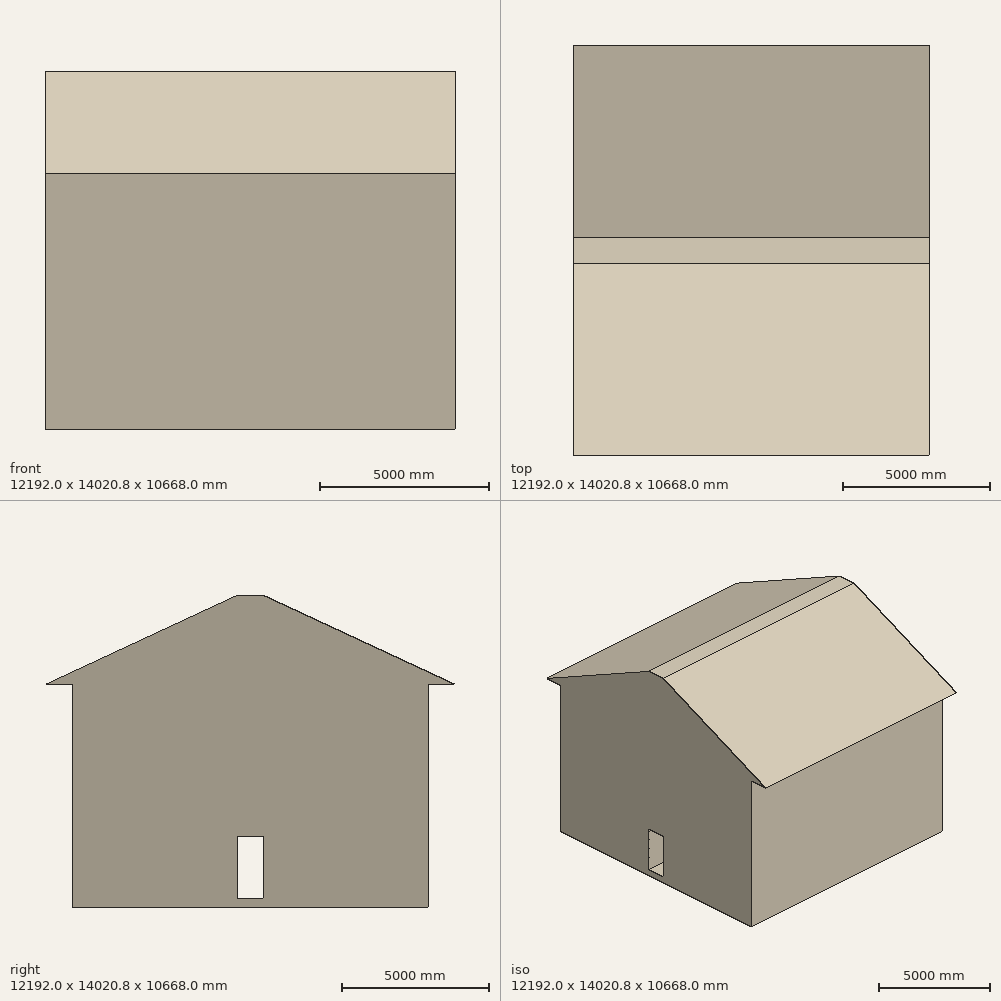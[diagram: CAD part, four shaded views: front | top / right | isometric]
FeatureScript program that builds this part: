
annotation { "Feature Type Name" : "Feature", "Feature Type Description" : "" }
export const myFeature = defineFeature(function(context is Context, id is Id, definition is map)
    precondition{}
    {
        {
            var Q0;
            Q0=qCreatedBy(makeId("Right.planeOp"),FACE);
            var sketch = newSketch(context, id + "F0", { "sketchPlane" : qUnion([Q0])});
            skLineSegment(sketch, "E0", {"start": v(0, 0) * mm, "end": v(-6096, 0) * mm});
            skLineSegment(sketch, "E1", {"start": v(0, 0) * mm, "end": v(6096, 0) * mm});
            skLineSegment(sketch, "E2", {"start": v(0, 0) * mm, "end": v(0, 3048) * mm, "construction": true});
            skLineSegment(sketch, "E3", {"start": v(-6096, 0) * mm, "end": v(0, 3048) * mm});
            skLineSegment(sketch, "E4", {"start": v(6096, 0) * mm, "end": v(0, 3048) * mm});
            skLineSegment(sketch, "E5", {"start": v(-6096, 0) * mm, "end": v(-6096, -7315.2) * mm});
            skLineSegment(sketch, "E6", {"start": v(-6096, -7315.2) * mm, "end": v(6096, -7315.2) * mm});
            skLineSegment(sketch, "E7", {"start": v(6096, 0) * mm, "end": v(6096, -7315.2) * mm});
            skLineSegment(sketch, "E8", {"start": v(-6096, -7315.2) * mm, "end": v(-6096, -7620) * mm});
            skLineSegment(sketch, "E9", {"start": v(-6096, -7620) * mm, "end": v(6096, -7620) * mm});
            skLineSegment(sketch, "E10", {"start": v(6096, -7620) * mm, "end": v(6096, -7315.2) * mm});
            skLineSegment(sketch, "E11", {"start": v(0, -7315.2) * mm, "end": v(-457.2, -7315.2) * mm});
            skLineSegment(sketch, "E12", {"start": v(0, -7315.2) * mm, "end": v(457.2, -7315.2) * mm});
            skLineSegment(sketch, "E13", {"start": v(-457.2, -7315.2) * mm, "end": v(-457.2, -5181.6) * mm});
            skLineSegment(sketch, "E14", {"start": v(-457.2, -5181.6) * mm, "end": v(457.2, -5181.6) * mm});
            skLineSegment(sketch, "E15", {"start": v(457.2, -5181.6) * mm, "end": v(457.2, -7315.2) * mm});
            skLineSegment(sketch, "E16", {"start": v(-6096, 0) * mm, "end": v(-7010.4, 0) * mm});
            skLineSegment(sketch, "E17", {"start": v(6096, 0) * mm, "end": v(7010.4, 0) * mm});
            skLineSegment(sketch, "E18", {"start": v(0, 3048) * mm, "end": v(457.2, 3048) * mm});
            skLineSegment(sketch, "E19", {"start": v(0, 3048) * mm, "end": v(-457.2, 3048) * mm});
            skLineSegment(sketch, "E20", {"start": v(-7010.4, 0) * mm, "end": v(-457.2, 3048) * mm});
            skLineSegment(sketch, "E21", {"start": v(7010.4, 0) * mm, "end": v(457.2, 3048) * mm});
            skLineSegment(sketch, "E22.bottom", {"start": v(-2743.2, -914.4) * mm, "end": v(-914.4, -914.4) * mm});
            skLineSegment(sketch, "E22.top", {"start": v(-2743.2, -2133.6) * mm, "end": v(-914.4, -2133.6) * mm});
            skLineSegment(sketch, "E22.left", {"start": v(-2743.2, -914.4) * mm, "end": v(-2743.2, -2133.6) * mm});
            skLineSegment(sketch, "E22.right", {"start": v(-914.4, -914.4) * mm, "end": v(-914.4, -2133.6) * mm});
            skLineSegment(sketch, "E23.bottom", {"start": v(3449.56, -218.05) * mm, "end": v(5278.36, -218.05) * mm});
            skLineSegment(sketch, "E23.top", {"start": v(3449.56, -1742.05) * mm, "end": v(5278.36, -1742.05) * mm});
            skLineSegment(sketch, "E23.left", {"start": v(3449.56, -218.05) * mm, "end": v(3449.56, -1742.05) * mm});
            skLineSegment(sketch, "E23.right", {"start": v(5278.36, -218.05) * mm, "end": v(5278.36, -1742.05) * mm});
            skLineSegment(sketch, "E24.bottom", {"start": v(-3558.79, -5153.92) * mm, "end": v(-2034.79, -5153.92) * mm});
            skLineSegment(sketch, "E24.top", {"start": v(-3558.79, -6677.92) * mm, "end": v(-2034.79, -6677.92) * mm});
            skLineSegment(sketch, "E24.left", {"start": v(-3558.79, -5153.92) * mm, "end": v(-3558.79, -6677.92) * mm});
            skLineSegment(sketch, "E24.right", {"start": v(-2034.79, -5153.92) * mm, "end": v(-2034.79, -6677.92) * mm});
            skLineSegment(sketch, "E25.left", {"start": v(-3558.79, -5153.92) * mm, "end": v(-3558.79, -5153.92) * mm});
            skCircle(sketch, "E26.cCircle", {"center": v(3162.99, -4421.52) * mm, "radius": 957.11 * mm, "construction": true});
            skLineSegment(sketch, "E26.0", {"start": v(4268.14, -4428.14) * mm, "end": v(3709.83, -5381.92) * mm});
            skLineSegment(sketch, "E26.1", {"start": v(3709.83, -5381.92) * mm, "end": v(2604.67, -5375.3) * mm});
            skLineSegment(sketch, "E26.2", {"start": v(2604.67, -5375.3) * mm, "end": v(2057.83, -4414.9) * mm});
            skLineSegment(sketch, "E26.3", {"start": v(2057.83, -4414.9) * mm, "end": v(2616.14, -3461.11) * mm});
            skLineSegment(sketch, "E26.4", {"start": v(2616.14, -3461.11) * mm, "end": v(3721.3, -3467.73) * mm});
            skLineSegment(sketch, "E26.5", {"start": v(3721.3, -3467.73) * mm, "end": v(4268.14, -4428.14) * mm});
            skPoint(sketch, "E26.0.midPoint", {"position": v(3988.99, -4905.03) * mm});
            skSolve(sketch);
        }
        {
            var Q0;
            {var subQ0=sQuery(id+"F0.wireOp",EDGE,"E8");Q0=makeQuery(id+"F0.imprint","IMPRINT",FACE,{"disambiguationData":[TD([[makeQuery(id+"F0.imprint","IMPRINT",EDGE,{"derivedFrom":subQ0}),1.0]])]});}
            var Q1;
            Q1=makeQuery(id+"F0.imprint","IMPRINT",FACE,{"disambiguationData":[TD([[makeQuery(id+"F0.imprint","IMPRINT",EDGE,{"derivedFrom":sQuery(id+"F0.wireOp",EDGE,"E3")}),1.0]])]});
            var Q2;
            Q2=makeQuery(id+"F0.imprint","IMPRINT",FACE,{"disambiguationData":[TD([[makeQuery(id+"F0.imprint","IMPRINT",EDGE,{"derivedFrom":sQuery(id+"F0.wireOp",EDGE,"E4")}),-1.0]])]});
            var Q3;
            Q3=makeQuery(id+"F0.imprint","IMPRINT",FACE,{"disambiguationData":[TD([[makeQuery(id+"F0.imprint","IMPRINT",EDGE,{"derivedFrom":sQuery(id+"F0.wireOp",EDGE,"E22.bottom")}),-1.0]])]});
            var Q4;
            Q4=makeQuery(id+"F0.imprint","IMPRINT",FACE,{"disambiguationData":[TD([[makeQuery(id+"F0.imprint","IMPRINT",EDGE,{"derivedFrom":sQuery(id+"F0.wireOp",EDGE,"E23.bottom")}),-1.0]])]});
            var Q5;
            Q5=makeQuery(id+"F0.imprint","IMPRINT",FACE,{"disambiguationData":[TD([[makeQuery(id+"F0.imprint","IMPRINT",EDGE,{"derivedFrom":sQuery(id+"F0.wireOp",EDGE,"E24.bottom")}),-1.0]])]});
            var Q6;
            Q6=makeQuery(id+"F0.imprint","IMPRINT",FACE,{"disambiguationData":[TD([[makeQuery(id+"F0.imprint","IMPRINT",EDGE,{"derivedFrom":sQuery(id+"F0.wireOp",EDGE,"E26.0")}),-1.0]])]});
            var Q7;
            Q7=makeQuery(id+"F0.imprint","IMPRINT",FACE,{"disambiguationData":[TD([[makeQuery(id+"F0.imprint","IMPRINT",EDGE,{"derivedFrom":sQuery(id+"F0.wireOp",EDGE,"E11")}),-1.0]])]});
            var Q8;
            Q8=makeQuery(id+"F0.imprint","IMPRINT",FACE,{"disambiguationData":[TD([[makeQuery(id+"F0.imprint","IMPRINT",EDGE,{"derivedFrom":sQuery(id+"F0.wireOp",EDGE,"E0")}),1.0]])]});
            var Q9;
            Q9=makeQuery(id+"F0.imprint","IMPRINT",FACE,{"disambiguationData":[TD([[makeQuery(id+"F0.imprint","IMPRINT",EDGE,{"derivedFrom":sQuery(id+"F0.wireOp",EDGE,"E0")}),-1.0]])]});
            extrude(context, id + "F1", {"entities" : qUnion([Q0, Q1, Q2, Q3, Q4, Q5, Q6, Q7, Q8, Q9]), "depth" : 12192 * mm, "offsetDistance" : 30.48 * mm});
        }
    });
